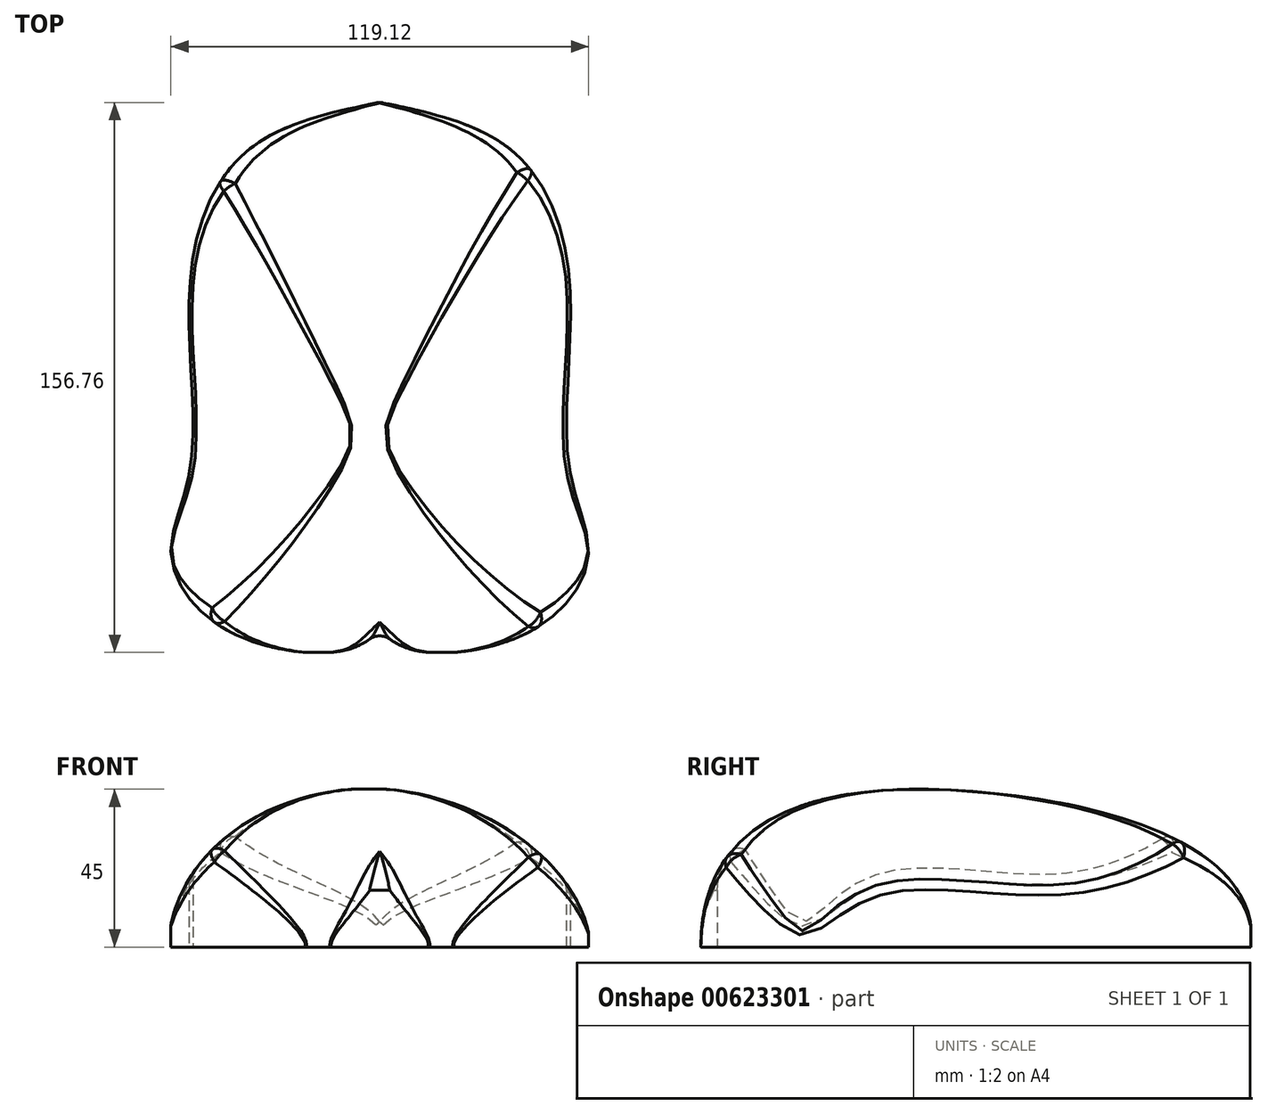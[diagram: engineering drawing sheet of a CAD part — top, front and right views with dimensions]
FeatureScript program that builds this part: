
annotation { "Feature Type Name" : "Feature", "Feature Type Description" : "" }
export const myFeature = defineFeature(function(context is Context, id is Id, definition is map)
    precondition{}
    {
        {
            var Q0;
            Q0=qCreatedBy(makeId("Top.planeOp"),FACE);
            var sketch = newSketch(context, id + "F0", { "sketchPlane" : qUnion([Q0])});
            skFitSpline(sketch, "E0", {"points": [v(0, 75.57) * mm, v(-37.55, 61.86) * mm, v(-54, 25.53) * mm, v(-54, -28.62) * mm, v(-59.48, -53.99) * mm, v(-43.03, -75.24) * mm, v(-10.13, -80.72) * mm, v(0, -75.24) * mm], "startDerivative": vector(-260.8, -53.97) * mm, "endDerivative": vector(93.06, 77.38) * mm});
            skFitSpline(sketch, "E1.MirrorCS", {"points": [v(0, 75.57) * mm, v(37.55, 61.86) * mm, v(54, 25.53) * mm, v(54, -28.62) * mm, v(59.48, -53.99) * mm, v(43.03, -75.24) * mm, v(10.13, -80.72) * mm, v(0, -75.24) * mm], "startDerivative": vector(260.8, -53.97) * mm, "endDerivative": vector(-93.06, 77.38) * mm});
            skSolve(sketch);
        }
        {
            var Q0;
            Q0=makeQuery(id+"F0.imprint","IMPRINT",FACE,{"disambiguationData":[TD([[makeQuery(id+"F0.imprint","IMPRINT",EDGE,{"derivedFrom":sQuery(id+"F0.wireOp",EDGE,"E0")}),1.0]])]});
            extrude(context, id + "F1", {"entities" : qUnion([Q0]), "depth" : 45.4 * mm, "offsetDistance" : 25 * mm});
        }
        {
            var Q0;
            Q0=qCreatedBy(makeId("Front.planeOp"),FACE);
            var sketch = newSketch(context, id + "F2", { "sketchPlane" : qUnion([Q0])});
            skFitSpline(sketch, "E2", {"points": [v(-60.5, 0) * mm, v(0, 45.1) * mm, v(60.15, 0) * mm], "startDerivative": vector(11.48, 172.76) * mm, "endDerivative": vector(11.5, -141.45) * mm});
            skLineSegment(sketch, "E3", {"start": v(-60.5, 0) * mm, "end": v(-60.5, 45.88) * mm});
            skLineSegment(sketch, "E4", {"start": v(-60.5, 45.88) * mm, "end": v(60.62, 45.88) * mm});
            skLineSegment(sketch, "E5", {"start": v(60.62, 45.88) * mm, "end": v(60.15, 0) * mm});
            skSolve(sketch);
        }
        {
            var Q0;
            Q0=makeQuery(id+"F2.imprint","IMPRINT",FACE,{"disambiguationData":[TD([[makeQuery(id+"F2.imprint","IMPRINT",EDGE,{"derivedFrom":sQuery(id+"F2.wireOp",EDGE,"E2")}),1.0]])]});
            extrude(context, id + "F3", {"entities" : qUnion([Q0]), "operationType" : NewBodyOperationType.REMOVE, "oppositeDirection" : true, "depth" : 108 * mm, "offsetDistance" : 25 * mm, "hasSecondDirection" : true, "secondDirectionOppositeDirection" : false, "secondDirectionDepth" : 139 * mm});
        }
        {
            var Q0;
            Q0=qCreatedBy(makeId("Right.planeOp"),FACE);
            var sketch = newSketch(context, id + "F4", { "sketchPlane" : qUnion([Q0])});
            skFitSpline(sketch, "E6", {"points": [v(-81.3, 0) * mm, v(0, 44.05) * mm, v(75.7, 0) * mm], "startDerivative": vector(0.13, 247.61) * mm, "endDerivative": vector(-15.26, -167.07) * mm});
            skLineSegment(sketch, "E7", {"start": v(-92.28, 48.28) * mm, "end": v(92.86, 48.28) * mm});
            skLineSegment(sketch, "E8", {"start": v(92.86, 48.28) * mm, "end": v(75.7, 0) * mm});
            skLineSegment(sketch, "E9", {"start": v(-81.3, 0) * mm, "end": v(-92.28, 0) * mm});
            skLineSegment(sketch, "E10", {"start": v(-92.28, 0) * mm, "end": v(-92.28, 48.28) * mm});
            skSolve(sketch);
        }
        {
            var Q0;
            Q0 = qSketchRegion(id + "F4", true);
            extrude(context, id + "F5", {"entities" : qUnion([Q0]), "operationType" : NewBodyOperationType.REMOVE, "oppositeDirection" : true, "depth" : 154 * mm, "offsetDistance" : 25 * mm, "hasSecondDirection" : true, "secondDirectionOppositeDirection" : false, "secondDirectionDepth" : 174 * mm});
        }
        {
            var Q0;
            {var subQ0=sQuery(id+"F4.wireOp",EDGE,"E6");Q0=makeQuery(id+"F5.boolean.opBoolean","INTERSECT",EDGE,{"disambiguationData":[OD(1.0)],"derivedFrom":[makeQuery(id+"F3.boolean.opBoolean","COPY",FACE,{"derivedFrom":makeQuery(id+"F3.opExtrude","SWEPT_FACE",FACE,{"disambiguationData":[OSD([sQuery(id+"F2.wireOp",EDGE,"E2")])]})}),makeQuery(id+"F5.opExtrude","SWEPT_FACE",FACE,{"disambiguationData":[OSD([subQ0]),TDD([makeQuery(id+"F4.imprint","IMPRINT",EDGE,{"disambiguationData":[TD([[makeQuery(id+"F4.imprint","INTERSECT",VERTEX,{"derivedFrom":[subQ0,sQuery(id+"F4.wireOp",EDGE,"G5fegEiq-ALTF-ZlPY-DPke-8hLnNe3T3628")]}),-1.0]])],"derivedFrom":subQ0})])]})]});}
            var Q1;
            {var subQ0=makeQuery(id+"F1.opExtrude","SWEPT_FACE",FACE,{"disambiguationData":[OSD([sQuery(id+"F0.wireOp",EDGE,"E1.MirrorCS")])]});var subQ1=makeQuery(id+"F3.opExtrude","SWEPT_FACE",FACE,{"disambiguationData":[OSD([sQuery(id+"F2.wireOp",EDGE,"E2")])]});var subQ2=sQuery(id+"F4.wireOp",EDGE,"E6");Q1=makeQuery(id+"F5.boolean.opBoolean","SPLIT",EDGE,{"disambiguationData":[TD([makeQuery(id+"F5.opExtrude","SWEPT_FACE",FACE,{"disambiguationData":[OSD([subQ2]),TDD([makeQuery(id+"F4.imprint","IMPRINT",EDGE,{"disambiguationData":[TD([[makeQuery(id+"F4.imprint","INTERSECT",VERTEX,{"derivedFrom":[subQ2,sQuery(id+"F4.wireOp",EDGE,"G5fegEiq-ALTF-ZlPY-DPke-8hLnNe3T3628")]}),-1.0]])],"derivedFrom":subQ2})])]})])],"derivedFrom":makeQuery(id+"F3.boolean.opBoolean","INTERSECT",EDGE,{"derivedFrom":[subQ0,subQ1]})});}
            var Q2;
            {var subQ0=sQuery(id+"F4.wireOp",EDGE,"E6");Q2=makeQuery(id+"F5.boolean.opBoolean","INTERSECT",EDGE,{"disambiguationData":[OD(0.0)],"derivedFrom":[makeQuery(id+"F1.opExtrude","SWEPT_FACE",FACE,{"disambiguationData":[OSD([sQuery(id+"F0.wireOp",EDGE,"E1.MirrorCS")])]}),makeQuery(id+"F5.opExtrude","SWEPT_FACE",FACE,{"disambiguationData":[OSD([subQ0]),TDD([makeQuery(id+"F4.imprint","IMPRINT",EDGE,{"disambiguationData":[TD([[makeQuery(id+"F4.imprint","INTERSECT",VERTEX,{"derivedFrom":[subQ0,sQuery(id+"F4.wireOp",EDGE,"G5fegEiq-ALTF-ZlPY-DPke-8hLnNe3T3628")]}),-1.0]])],"derivedFrom":subQ0})])]})]});}
            fillet(context, id + "F6", {"entities" : qUnion([Q0, Q1, Q2]), "radius" : 5 * mm, "tangentPropagation" : true, "allowEdgeOverflow" : false});
        }
        {
            var Q0;
            Q0=makeQuery(id+"F3.boolean.opBoolean","INTERSECT",EDGE,{"derivedFrom":[makeQuery(id+"F1.opExtrude","SWEPT_FACE",FACE,{"disambiguationData":[OSD([sQuery(id+"F0.wireOp",EDGE,"E0")])]}),makeQuery(id+"F3.opExtrude","SWEPT_FACE",FACE,{"disambiguationData":[OSD([sQuery(id+"F2.wireOp",EDGE,"E2")])]})]});
            var Q1;
            Q1=makeQuery(id+"F5.boolean.opBoolean","INTERSECT",EDGE,{"disambiguationData":[OD(0.0)],"derivedFrom":[makeQuery(id+"F1.opExtrude","SWEPT_FACE",FACE,{"disambiguationData":[OSD([sQuery(id+"F0.wireOp",EDGE,"E0")])]}),makeQuery(id+"F5.opExtrude","SWEPT_FACE",FACE,{"disambiguationData":[OSD([sQuery(id+"F4.wireOp",EDGE,"E6")])]})]});
            var Q2;
            Q2=makeQuery(id+"F5.boolean.opBoolean","INTERSECT",EDGE,{"disambiguationData":[OD(0.0)],"derivedFrom":[makeQuery(id+"F3.boolean.opBoolean","COPY",FACE,{"derivedFrom":makeQuery(id+"F3.opExtrude","SWEPT_FACE",FACE,{"disambiguationData":[OSD([sQuery(id+"F2.wireOp",EDGE,"E2")])]})}),makeQuery(id+"F5.opExtrude","SWEPT_FACE",FACE,{"disambiguationData":[OSD([sQuery(id+"F4.wireOp",EDGE,"E6")])]})]});
            var Q3;
            Q3=makeQuery(id+"F5.boolean.opBoolean","INTERSECT",EDGE,{"disambiguationData":[OD(2.0)],"derivedFrom":[makeQuery(id+"F1.opExtrude","SWEPT_FACE",FACE,{"disambiguationData":[OSD([sQuery(id+"F0.wireOp",EDGE,"E0")])]}),makeQuery(id+"F5.opExtrude","SWEPT_FACE",FACE,{"disambiguationData":[OSD([sQuery(id+"F4.wireOp",EDGE,"E6")])]})]});
            fillet(context, id + "F7", {"entities" : qUnion([Q0, Q1, Q2, Q3]), "radius" : 5 * mm, "tangentPropagation" : true, "allowEdgeOverflow" : false});
        }
        {
            var Q0;
            {var subQ0=sQuery(id+"F0.wireOp",EDGE,"E1.MirrorCS");var subQ1=sQuery(id+"F0.wireOp",EDGE,"E0");Q0=makeQuery(id+"F1.opExtrude","SWEPT_EDGE",EDGE,{"disambiguationData":[OSD([subQ1,subQ0]),TDD([makeQuery(id+"F0.imprint","INTERSECT",VERTEX,{"disambiguationData":[OD(1.0)],"derivedFrom":[subQ1,subQ0]})])]});}
            var Q1;
            Q1=makeQuery(id+"F5.boolean.opBoolean","INTERSECT",EDGE,{"disambiguationData":[OD(1.0)],"derivedFrom":[makeQuery(id+"F1.opExtrude","SWEPT_FACE",FACE,{"disambiguationData":[OSD([sQuery(id+"F0.wireOp",EDGE,"E0")])]}),makeQuery(id+"F5.opExtrude","SWEPT_FACE",FACE,{"disambiguationData":[OSD([sQuery(id+"F4.wireOp",EDGE,"E6")])]})]});
            fillet(context, id + "F8", {"entities" : qUnion([Q0, Q1]), "radius" : 5 * mm, "tangentPropagation" : true, "allowEdgeOverflow" : false});
        }
    });
